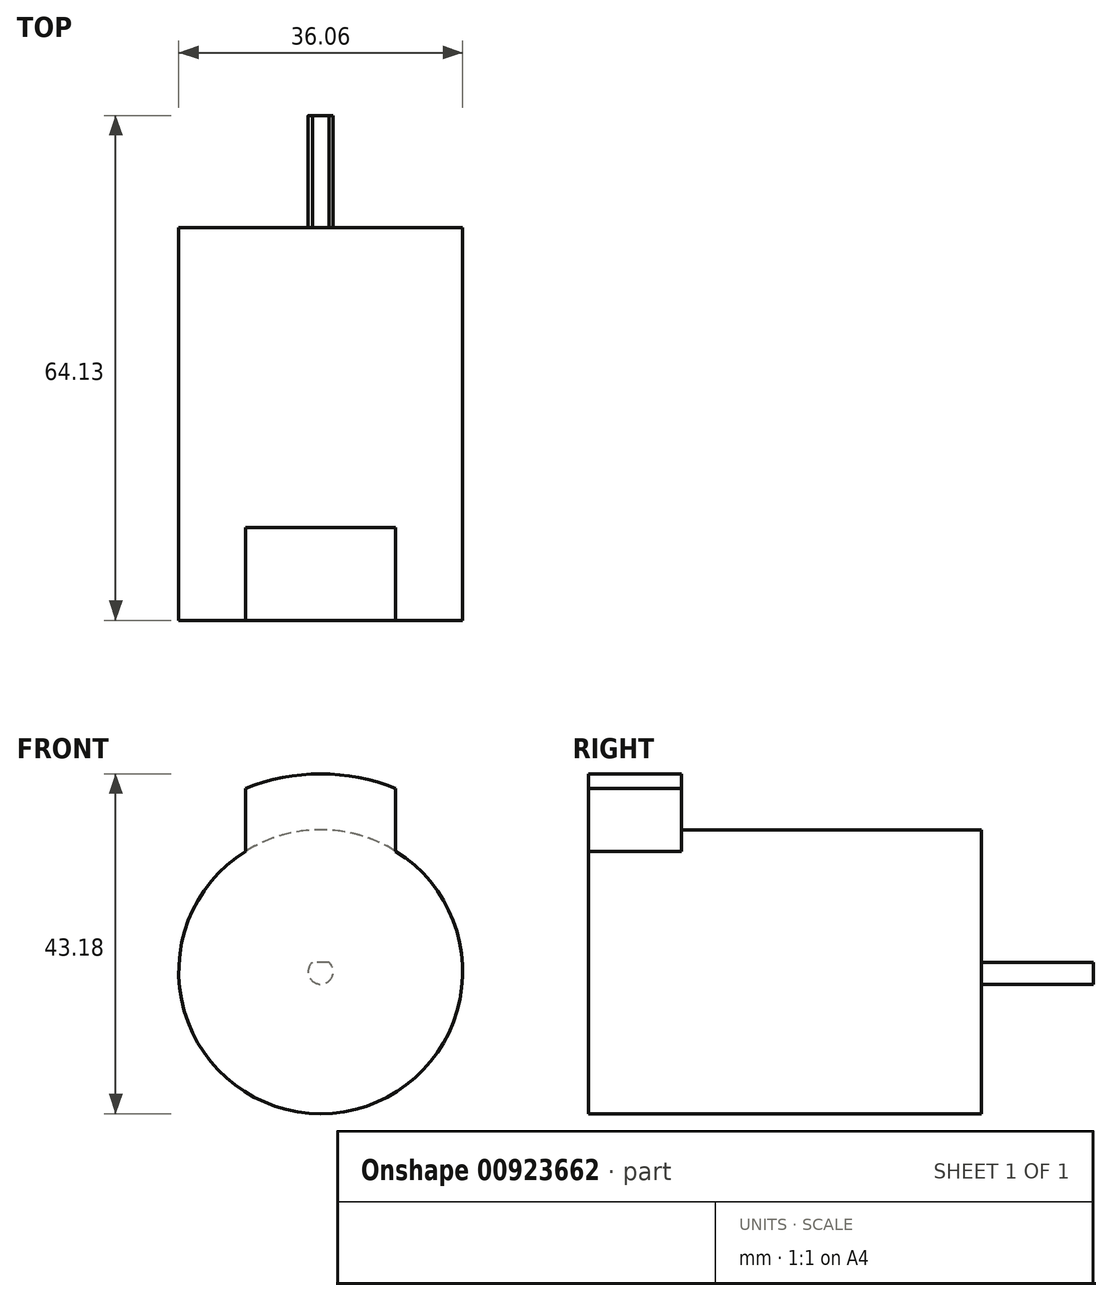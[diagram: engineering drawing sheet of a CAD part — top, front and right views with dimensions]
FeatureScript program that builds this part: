
annotation { "Feature Type Name" : "Feature", "Feature Type Description" : "" }
export const myFeature = defineFeature(function(context is Context, id is Id, definition is map)
    precondition{}
    {
        {
            var Q0;
            Q0=qCreatedBy(makeId("Front.planeOp"),FACE);
            var sketch = newSketch(context, id + "F0", { "sketchPlane" : qUnion([Q0])});
            skCircle(sketch, "E0", {"center": v(0, 0) * mm, "radius": 18.03 * mm});
            skSolve(sketch);
        }
        {
            var Q0;
            Q0 = qSketchRegion(id + "F0", true);
            extrude(context, id + "F1", {"entities" : qUnion([Q0]), "oppositeDirection" : true, "depth" : 49.9 * mm, "offsetDistance" : 25.4 * mm});
        }
        {
            var Q0;
            Q0=qCreatedBy(makeId("Front.planeOp"),FACE);
            var sketch = newSketch(context, id + "F2", { "sketchPlane" : qUnion([Q0])});
            skArc(sketch, "E1.0", {"start": v(9.53, 15.31) * mm, "mid": v(0, 18.03) * mm, "end": v(-9.53, 15.31) * mm});
            skLineSegment(sketch, "E2", {"start": v(0, 0) * mm, "end": v(0, 56.6) * mm, "construction": true});
            skArc(sketch, "E3", {"start": v(9.53, 23.27) * mm, "mid": v(4.85, 24.67) * mm, "end": v(0, 25.15) * mm});
            skLineSegment(sketch, "E4", {"start": v(9.53, 15.31) * mm, "end": v(9.53, 23.27) * mm});
            skArc(sketch, "E5.MirrorCS", {"start": v(-9.53, 23.27) * mm, "mid": v(-4.85, 24.67) * mm, "end": v(0, 25.15) * mm});
            skLineSegment(sketch, "E6.MirrorCS", {"start": v(-9.53, 15.31) * mm, "end": v(-9.53, 23.27) * mm});
            skSolve(sketch);
        }
        {
            var Q0;
            Q0 = qSketchRegion(id + "F2", true);
            extrude(context, id + "F3", {"entities" : qUnion([Q0]), "operationType" : NewBodyOperationType.ADD, "oppositeDirection" : true, "depth" : 11.8 * mm, "offsetDistance" : 25.4 * mm});
        }
        {
            var Q0;
            Q0=makeQuery(id+"F1.opExtrude","CAP_FACE",FACE,{"disambiguationData":[OSD([sQuery(id+"F0.wireOp",EDGE,"E0")])],"isStart":false});
            var sketch = newSketch(context, id + "F4", { "sketchPlane" : qUnion([Q0])});
            skArc(sketch, "E7", {"start": v(-1.03, 1.2) * mm, "mid": v(0, -1.59) * mm, "end": v(1.03, 1.2) * mm});
            skLineSegment(sketch, "E8", {"start": v(-1.03, 1.2) * mm, "end": v(1.03, 1.2) * mm});
            skSolve(sketch);
        }
        {
            var Q0;
            Q0 = qSketchRegion(id + "F4", true);
            extrude(context, id + "F5", {"entities" : qUnion([Q0]), "operationType" : NewBodyOperationType.ADD, "depth" : 14.22 * mm, "offsetDistance" : 25.4 * mm});
        }
    });
